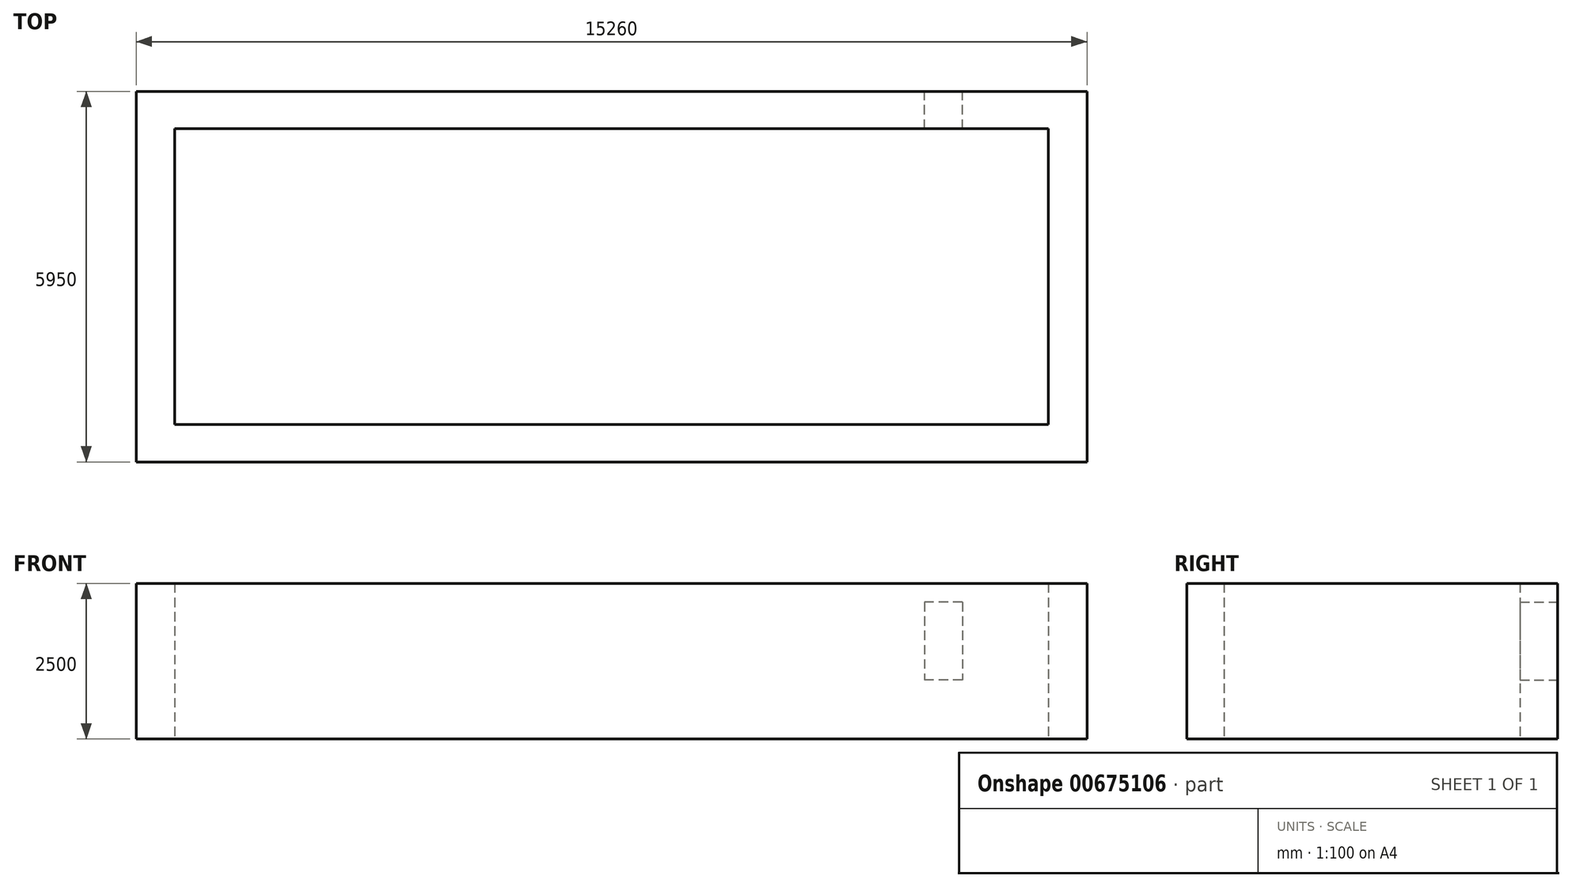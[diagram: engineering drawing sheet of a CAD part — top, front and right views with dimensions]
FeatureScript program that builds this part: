
annotation { "Feature Type Name" : "Feature", "Feature Type Description" : "" }
export const myFeature = defineFeature(function(context is Context, id is Id, definition is map)
    precondition{}
    {
        {
            var Q0;
            Q0=qCreatedBy(makeId("Top.planeOp"),FACE);
            var sketch = newSketch(context, id + "F0", { "sketchPlane" : qUnion([Q0])});
            skLineSegment(sketch, "E0.bottom", {"start": v(7630, 2975) * mm, "end": v(-7630, 2975) * mm});
            skLineSegment(sketch, "E0.top", {"start": v(7630, -2975) * mm, "end": v(-7630, -2975) * mm});
            skLineSegment(sketch, "E0.left", {"start": v(7630, 2975) * mm, "end": v(7630, -2975) * mm});
            skLineSegment(sketch, "E0.right", {"start": v(-7630, 2975) * mm, "end": v(-7630, -2975) * mm});
            skPoint(sketch, "E0.middle", {"position": v(0, 0) * mm});
            skLineSegment(sketch, "E1.bottom", {"start": v(7010, 2375) * mm, "end": v(-7010, 2375) * mm});
            skLineSegment(sketch, "E1.top", {"start": v(7010, -2375) * mm, "end": v(-7010, -2375) * mm});
            skLineSegment(sketch, "E1.left", {"start": v(7010, 2375) * mm, "end": v(7010, -2375) * mm});
            skLineSegment(sketch, "E1.right", {"start": v(-7010, 2375) * mm, "end": v(-7010, -2375) * mm});
            skSolve(sketch);
        }
        {
            var Q0;
            Q0 = qSketchRegion(id + "F0", true);
            extrude(context, id + "F1", {"entities" : qUnion([Q0]), "depth" : 2500 * mm, "offsetDistance" : 25 * mm});
        }
        {
            var Q0;
            Q0=makeQuery(id+"F1.opExtrude","SWEPT_FACE",FACE,{"disambiguationData":[OSD([sQuery(id+"F0.wireOp",EDGE,"E0.bottom")])]});
            var sketch = newSketch(context, id + "F2", { "sketchPlane" : qUnion([Q0])});
            skLineSegment(sketch, "E2.bottom", {"start": v(-5630.13, 2200) * mm, "end": v(-5020.13, 2200) * mm});
            skLineSegment(sketch, "E2.top", {"start": v(-5630.13, 950) * mm, "end": v(-5020.13, 950) * mm});
            skLineSegment(sketch, "E2.left", {"start": v(-5630.13, 2200) * mm, "end": v(-5630.13, 950) * mm});
            skLineSegment(sketch, "E2.right", {"start": v(-5020.13, 2200) * mm, "end": v(-5020.13, 950) * mm});
            skSolve(sketch);
        }
        {
            var Q0;
            Q0 = qSketchRegion(id + "F2", true);
            extrude(context, id + "F3", {"entities" : qUnion([Q0]), "operationType" : NewBodyOperationType.REMOVE, "endBound" : BoundingType.UP_TO_NEXT, "oppositeDirection" : true, "depth" : 25 * mm, "offsetDistance" : 25 * mm});
        }
    });
